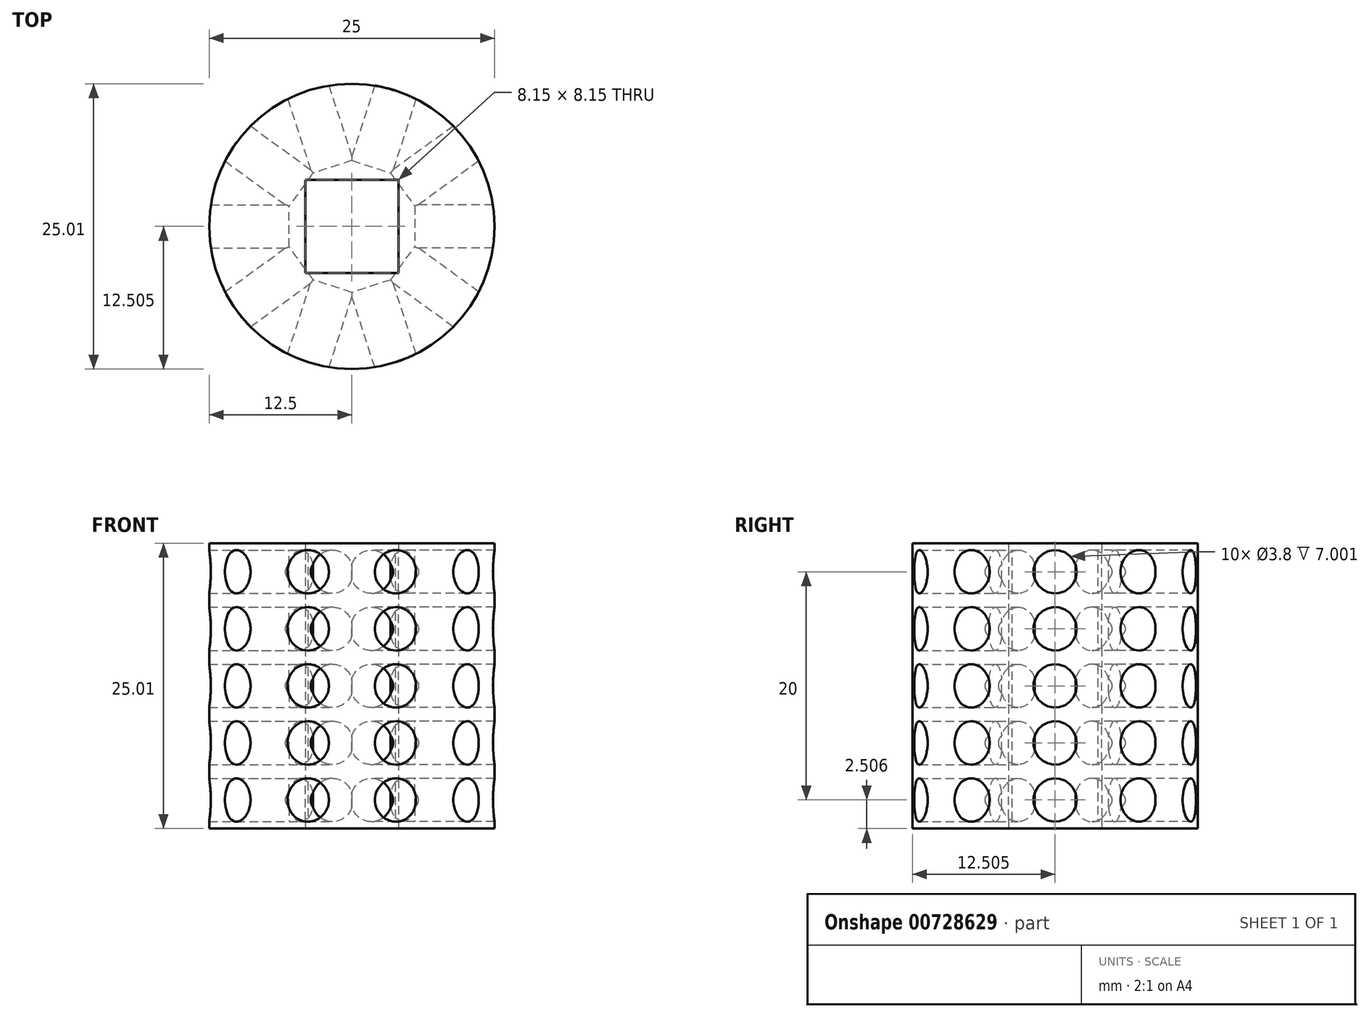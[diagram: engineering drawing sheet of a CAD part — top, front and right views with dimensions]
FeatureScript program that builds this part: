
annotation { "Feature Type Name" : "Feature", "Feature Type Description" : "" }
export const myFeature = defineFeature(function(context is Context, id is Id, definition is map)
    precondition{}
    {
        {
            var Q0;
            Q0=qCreatedBy(makeId("Front.planeOp"),FACE);
            var sketch = newSketch(context, id + "F0", { "sketchPlane" : qUnion([Q0])});
            skCircle(sketch, "E0", {"center": v(0, 0) * mm, "radius": 12.5 * mm});
            skLineSegment(sketch, "E1.bottom", {"start": v(4.08, -4.07) * mm, "end": v(-4.08, -4.08) * mm});
            skLineSegment(sketch, "E1.top", {"start": v(4.08, 4.08) * mm, "end": v(-4.07, 4.07) * mm});
            skLineSegment(sketch, "E1.left", {"start": v(4.08, -4.07) * mm, "end": v(4.08, 4.08) * mm});
            skLineSegment(sketch, "E1.right", {"start": v(-4.08, -4.08) * mm, "end": v(-4.08, 4.07) * mm});
            skSolve(sketch);
        }
        {
            var Q0;
            Q0=qSketchRegion(id+"F0",true);
            extrude(context, id + "F1", {"entities" : qUnion([Q0]), "depth" : 25 * mm, "offsetDistance" : 25 * mm});
        }
        {
            var Q0;
            Q0=qCreatedBy(makeId("Right.planeOp"),FACE);
            var sketch = newSketch(context, id + "F2", { "sketchPlane" : qUnion([Q0])});
            skCircle(sketch, "E2", {"center": v(-17.5, 0) * mm, "radius": 1.9 * mm});
            skCircle(sketch, "E3", {"center": v(-12.5, 0) * mm, "radius": 1.9 * mm});
            skCircle(sketch, "E4", {"center": v(-7.5, 0) * mm, "radius": 1.9 * mm});
            skCircle(sketch, "E5", {"center": v(-2.5, 0) * mm, "radius": 1.9 * mm});
            skLineSegment(sketch, "E6", {"start": v(-17.5, 0) * mm, "end": v(-12.5, 0) * mm});
            skLineSegment(sketch, "E7", {"start": v(-7.5, 0) * mm, "end": v(-12.5, 0) * mm});
            skLineSegment(sketch, "E8", {"start": v(-7.5, 0) * mm, "end": v(-2.5, 0) * mm});
            skCircle(sketch, "E9", {"center": v(-22.5, 0) * mm, "radius": 1.9 * mm});
            skLineSegment(sketch, "E10", {"start": v(-17.5, 0) * mm, "end": v(-22.5, 0) * mm});
            skSolve(sketch);
        }
        {
            var Q0;
            Q0 = qSketchRegion(id + "F2", true);
            extrude(context, id + "F3", {"entities" : qUnion([Q0]), "depth" : (14.5) * mm, "offsetDistance" : 25 * mm, "hasSecondDirection" : true, "secondDirectionOppositeDirection" : true, "secondDirectionDepth" : (-25 / 2 + 7) * mm});
        }
        {
            var Q0;
            Q0=qCreatedBy(makeId("Top.planeOp"),FACE);
            var sketch = newSketch(context, id + "F4", { "sketchPlane" : qUnion([Q0])});
            skLineSegment(sketch, "E11", {"start": v(0, 0) * mm, "end": v(0, -39.36) * mm});
            skSolve(sketch);
        }
        {
            var Q0;
            Q0=makeQuery(id+"F3.opExtrude","SWEPT_BODY",BODY,{"disambiguationData":[OSD([sQuery(id+"F2.wireOp",EDGE,"E9")])]});
            var Q1;
            Q1=makeQuery(id+"F3.opExtrude","SWEPT_BODY",BODY,{"disambiguationData":[OSD([sQuery(id+"F2.wireOp",EDGE,"E2")])]});
            var Q2;
            Q2=makeQuery(id+"F3.opExtrude","SWEPT_BODY",BODY,{"disambiguationData":[OSD([sQuery(id+"F2.wireOp",EDGE,"E3")])]});
            var Q3;
            Q3=makeQuery(id+"F3.opExtrude","SWEPT_BODY",BODY,{"disambiguationData":[OSD([sQuery(id+"F2.wireOp",EDGE,"E4")])]});
            var Q4;
            Q4=makeQuery(id+"F3.opExtrude","SWEPT_BODY",BODY,{"disambiguationData":[OSD([sQuery(id+"F2.wireOp",EDGE,"E5")])]});
            var Q5;
            Q5=makeQuery(id+"F3.opExtrude","SWEPT_BODY",BODY,{"disambiguationData":[OSD([sQuery(id+"F2.wireOp",EDGE,"WpjTBmhx-za1b-hTiM-c20u-NwAHVD54b8k5")])]});
            var Q6;
            Q6=makeQuery(id+"F3.opExtrude","SWEPT_FACE",FACE,{"disambiguationData":[OSD([sQuery(id+"F2.wireOp",EDGE,"E9")])]});
            var Q7;
            Q7=makeQuery(id+"F3.opExtrude","SWEPT_FACE",FACE,{"disambiguationData":[OSD([sQuery(id+"F2.wireOp",EDGE,"E2")])]});
            var Q8;
            Q8=makeQuery(id+"F3.opExtrude","SWEPT_FACE",FACE,{"disambiguationData":[OSD([sQuery(id+"F2.wireOp",EDGE,"E3")])]});
            var Q9;
            Q9=makeQuery(id+"F3.opExtrude","SWEPT_FACE",FACE,{"disambiguationData":[OSD([sQuery(id+"F2.wireOp",EDGE,"E4")])]});
            var Q10;
            Q10=makeQuery(id+"F3.opExtrude","SWEPT_FACE",FACE,{"disambiguationData":[OSD([sQuery(id+"F2.wireOp",EDGE,"E5")])]});
            var Q11;
            Q11=makeQuery(id+"F3.opExtrude","SWEPT_FACE",FACE,{"disambiguationData":[OSD([sQuery(id+"F2.wireOp",EDGE,"WpjTBmhx-za1b-hTiM-c20u-NwAHVD54b8k5")])]});
            var Q12;
            Q12=sQuery(id+"F4.wireOp",EDGE,"E11");
            circularPattern(context, id + "F5", {"operationType" : NewBodyOperationType.REMOVE, "entities" : qUnion([Q0, Q1, Q2, Q3, Q4, Q5]), "axis" : qUnion([Q12]), "angle" : 360 * degree, "instanceCount" : 10, "equalSpace" : true});
        }
        {
            var Q0;
            Q0=makeQuery(id+"F1.opExtrude","SWEPT_BODY",BODY,{"disambiguationData":[OSD([sQuery(id+"F0.wireOp",EDGE,"E0"),sQuery(id+"F0.wireOp",EDGE,"E1.bottom"),sQuery(id+"F0.wireOp",EDGE,"E1.top"),sQuery(id+"F0.wireOp",EDGE,"E1.left"),sQuery(id+"F0.wireOp",EDGE,"E1.right")])]});
            var Q1;
            Q1=makeQuery(id+"F1.opExtrude","CAP_EDGE",EDGE,{"disambiguationData":[OSD([sQuery(id+"F0.wireOp",EDGE,"E1.bottom")])],"isStart":true});
            transform(context, id + "F6", {"entities" : qUnion([Q0]), "transformType" : TransformType.ROTATION, "transformAxis" : qUnion([Q1]), "angle" : 90 * degree, "makeCopy" : false});
        }
    });
